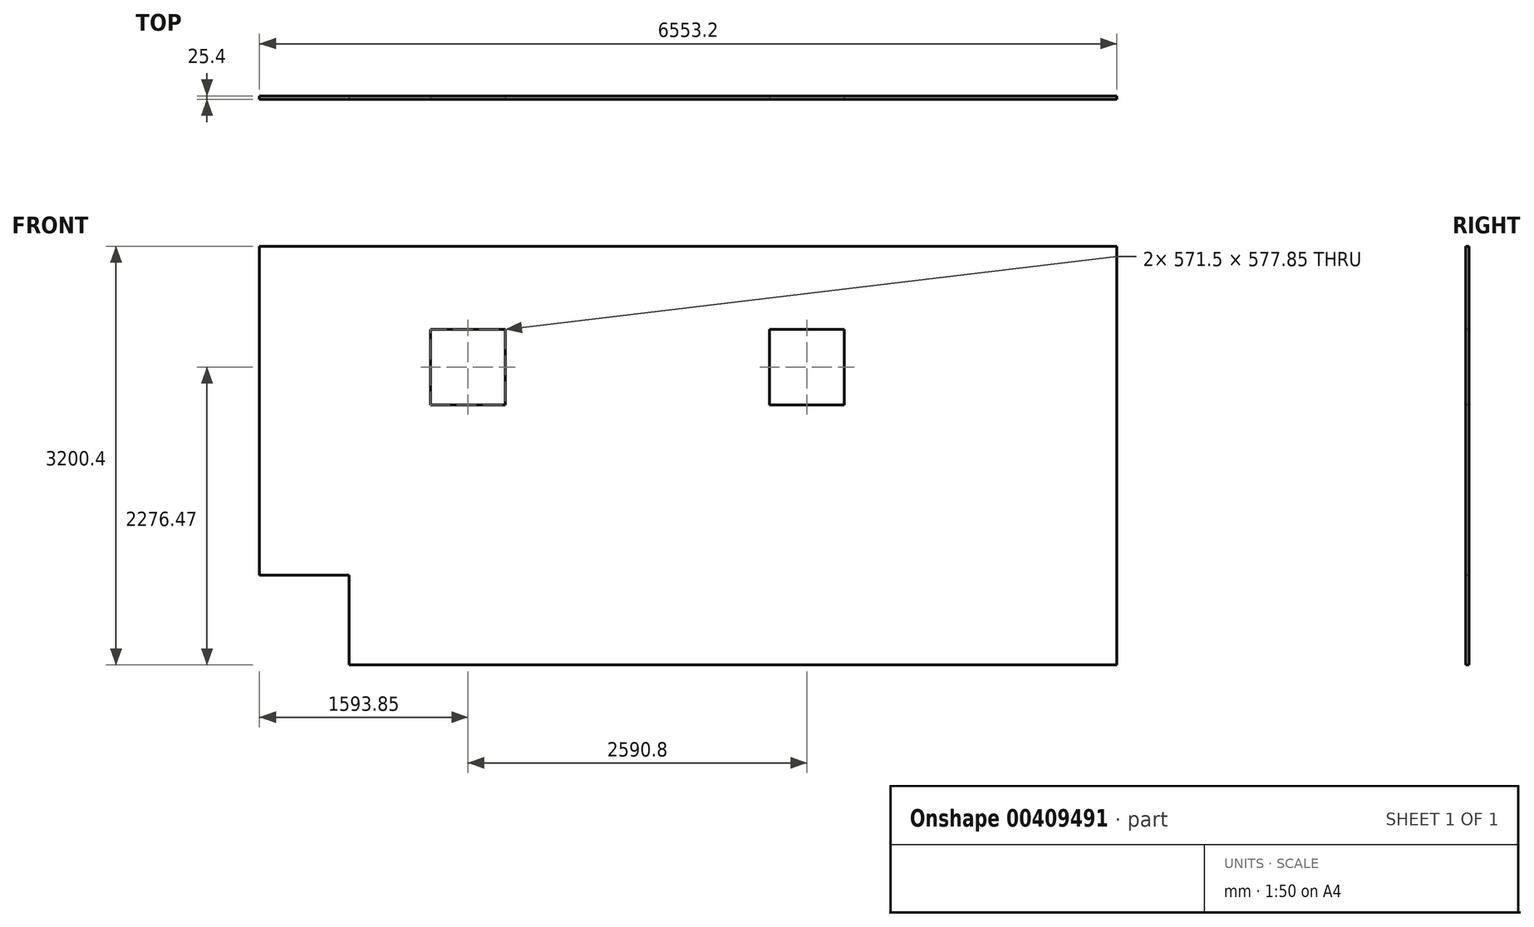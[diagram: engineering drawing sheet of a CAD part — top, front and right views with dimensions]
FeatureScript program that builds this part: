
annotation { "Feature Type Name" : "Feature", "Feature Type Description" : "" }
export const myFeature = defineFeature(function(context is Context, id is Id, definition is map)
    precondition{}
    {
        {
            var Q0;
            Q0=qCreatedBy(makeId("Front.planeOp"),FACE);
            var sketch = newSketch(context, id + "F0", { "sketchPlane" : qUnion([Q0])});
            skLineSegment(sketch, "E0", {"start": v(0, -1600.2) * mm, "end": v(3276.6, -1600.2) * mm});
            skLineSegment(sketch, "E1", {"start": v(3276.6, -1600.2) * mm, "end": v(3276.6, 1600.2) * mm});
            skLineSegment(sketch, "E2", {"start": v(3276.6, 1600.2) * mm, "end": v(0, 1600.2) * mm});
            skLineSegment(sketch, "E3", {"start": v(0, -1600.2) * mm, "end": v(-2590.8, -1600.2) * mm});
            skLineSegment(sketch, "E4", {"start": v(-2590.8, -1600.2) * mm, "end": v(-2590.8, -914.4) * mm});
            skLineSegment(sketch, "E5", {"start": v(-2590.8, -914.4) * mm, "end": v(-3276.6, -914.4) * mm});
            skLineSegment(sketch, "E6", {"start": v(-3276.6, -914.4) * mm, "end": v(-3276.6, 1600.2) * mm});
            skLineSegment(sketch, "E7", {"start": v(0, 1600.2) * mm, "end": v(-3276.6, 1600.2) * mm});
            skLineSegment(sketch, "E8.MirrorCS", {"start": v(622.3, 965.2) * mm, "end": v(622.3, 387.35) * mm});
            skLineSegment(sketch, "E9.MirrorCS", {"start": v(1193.8, 965.2) * mm, "end": v(1193.8, 387.35) * mm});
            skLineSegment(sketch, "E10.MirrorCS", {"start": v(1193.8, 965.2) * mm, "end": v(622.3, 965.2) * mm});
            skLineSegment(sketch, "E11.MirrorCS", {"start": v(1193.8, 387.35) * mm, "end": v(622.3, 387.35) * mm});
            skLineSegment(sketch, "E12.bottom", {"start": v(-1968.5, 965.2) * mm, "end": v(-1397, 965.2) * mm});
            skLineSegment(sketch, "E12.top", {"start": v(-1968.5, 387.35) * mm, "end": v(-1397, 387.35) * mm});
            skLineSegment(sketch, "E12.left", {"start": v(-1968.5, 965.2) * mm, "end": v(-1968.5, 387.35) * mm});
            skLineSegment(sketch, "E12.right", {"start": v(-1397, 965.2) * mm, "end": v(-1397, 387.35) * mm});
            skSolve(sketch);
        }
        {
            var Q0;
            Q0=makeQuery(id+"F0.imprint","IMPRINT",FACE,{"disambiguationData":[TD([[makeQuery(id+"F0.imprint","IMPRINT",EDGE,{"derivedFrom":sQuery(id+"F0.wireOp",EDGE,"E0")}),1.0]])]});
            extrude(context, id + "F1", {"entities" : qUnion([Q0]), "oppositeDirection" : true, "depth" : 25.4 * mm});
        }
    });
